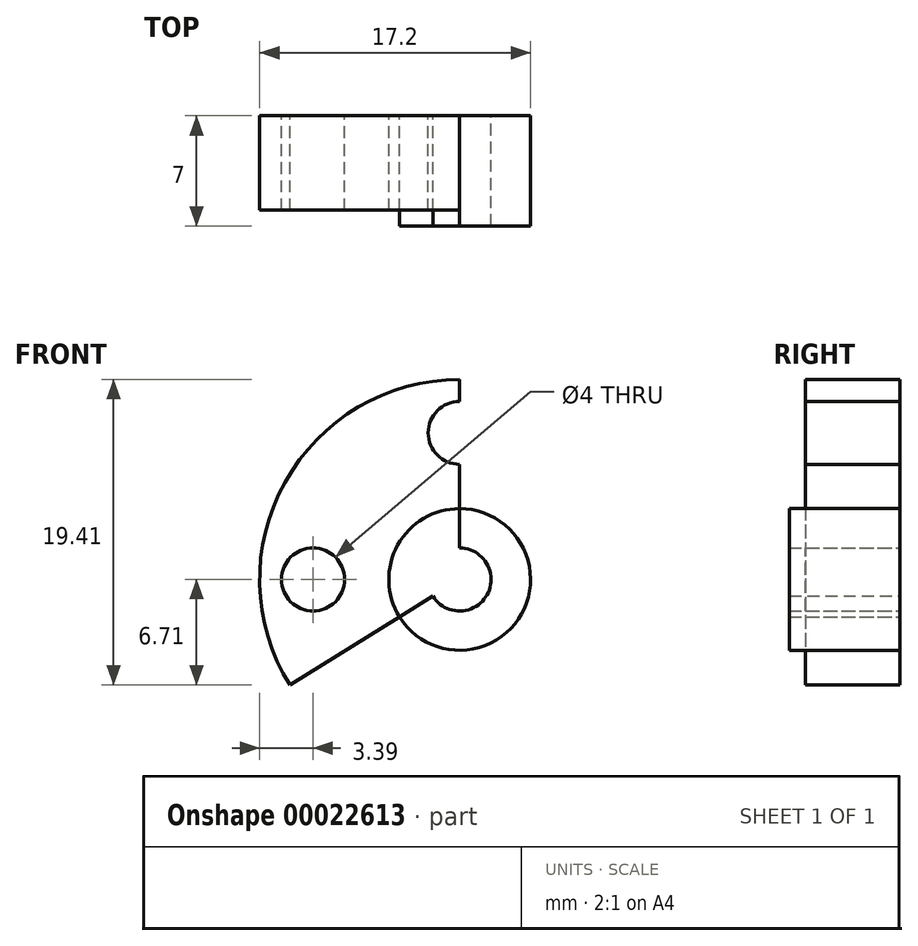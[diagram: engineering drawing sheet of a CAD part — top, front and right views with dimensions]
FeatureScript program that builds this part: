
annotation { "Feature Type Name" : "Feature", "Feature Type Description" : "" }
export const myFeature = defineFeature(function(context is Context, id is Id, definition is map)
    precondition{}
    {
        {
            var Q0;
            Q0=qCreatedBy(makeId("Front.planeOp"),FACE);
            var sketch = newSketch(context, id + "F0", { "sketchPlane" : qUnion([Q0])});
            skCircle(sketch, "E0", {"center": v(0, 0) * mm, "radius": 12.7 * mm});
            skLineSegment(sketch, "E1", {"start": v(0, 0) * mm, "end": v(0, 12.7) * mm});
            skCircle(sketch, "E2", {"center": v(0, 0) * mm, "radius": 4.5 * mm});
            skCircle(sketch, "E3", {"center": v(0, 9.31) * mm, "radius": 2 * mm});
            skCircle(sketch, "E4.1.0", {"center": v(-9.31, 0) * mm, "radius": 2 * mm});
            skCircle(sketch, "E4.2.0", {"center": v(0, -9.31) * mm, "radius": 2 * mm});
            skCircle(sketch, "E4.3.0", {"center": v(9.31, 0) * mm, "radius": 2 * mm});
            skLineSegment(sketch, "E5", {"start": v(-2, 9.35) * mm, "end": v(2, 9.31) * mm});
            skLineSegment(sketch, "E6", {"start": v(0, -4.5) * mm, "end": v(0, 4.5) * mm});
            skCircle(sketch, "E7", {"center": v(0, 0) * mm, "radius": 2 * mm});
            skLineSegment(sketch, "E8", {"start": v(0, 0) * mm, "end": v(2, 0) * mm});
            skLineSegment(sketch, "E9", {"start": v(0, 0) * mm, "end": v(-10.78, -6.71) * mm});
            skSolve(sketch);
        }
        {
            var Q0;
            Q0=makeQuery(id+"F0.imprint","IMPRINT",FACE,{"disambiguationData":[TD([[makeQuery(id+"F0.imprint","IMPRINT",EDGE,{"derivedFrom":sQuery(id+"F0.wireOp",EDGE,"E0")}),1.0]])]});
            extrude(context, id + "F1", {"entities" : qUnion([Q0]), "depth" : 6 * mm});
        }
        {
            var Q0;
            {var subQ0=sQuery(id+"F0.wireOp",EDGE,"E6");var subQ3=sQuery(id+"F0.wireOp",EDGE,"E2");var subQ4=makeQuery(id+"F0.imprint","INTERSECT",VERTEX,{"disambiguationData":[OD(0.0)],"derivedFrom":[subQ3,subQ0]});Q0=makeQuery(id+"F0.imprint","IMPRINT",FACE,{"disambiguationData":[TD([[makeQuery(id+"F0.imprint","IMPRINT",EDGE,{"disambiguationData":[TD([[subQ4,-1.0]])],"derivedFrom":subQ3}),1.0]])]});}
            var Q1;
            {var subQ1=sQuery(id+"F0.wireOp",EDGE,"E6");var subQ5=sQuery(id+"F0.wireOp",EDGE,"E2");var subQ6=makeQuery(id+"F0.imprint","INTERSECT",VERTEX,{"disambiguationData":[OD(0.0)],"derivedFrom":[subQ5,subQ1]});Q1=makeQuery(id+"F0.imprint","IMPRINT",FACE,{"disambiguationData":[TD([[makeQuery(id+"F0.imprint","IMPRINT",EDGE,{"disambiguationData":[TD([[subQ6,1.0]])],"derivedFrom":subQ5}),1.0]])]});}
            extrude(context, id + "F2", {"entities" : qUnion([Q0, Q1]), "operationType" : NewBodyOperationType.ADD, "depth" : 7 * mm});
        }
    });
